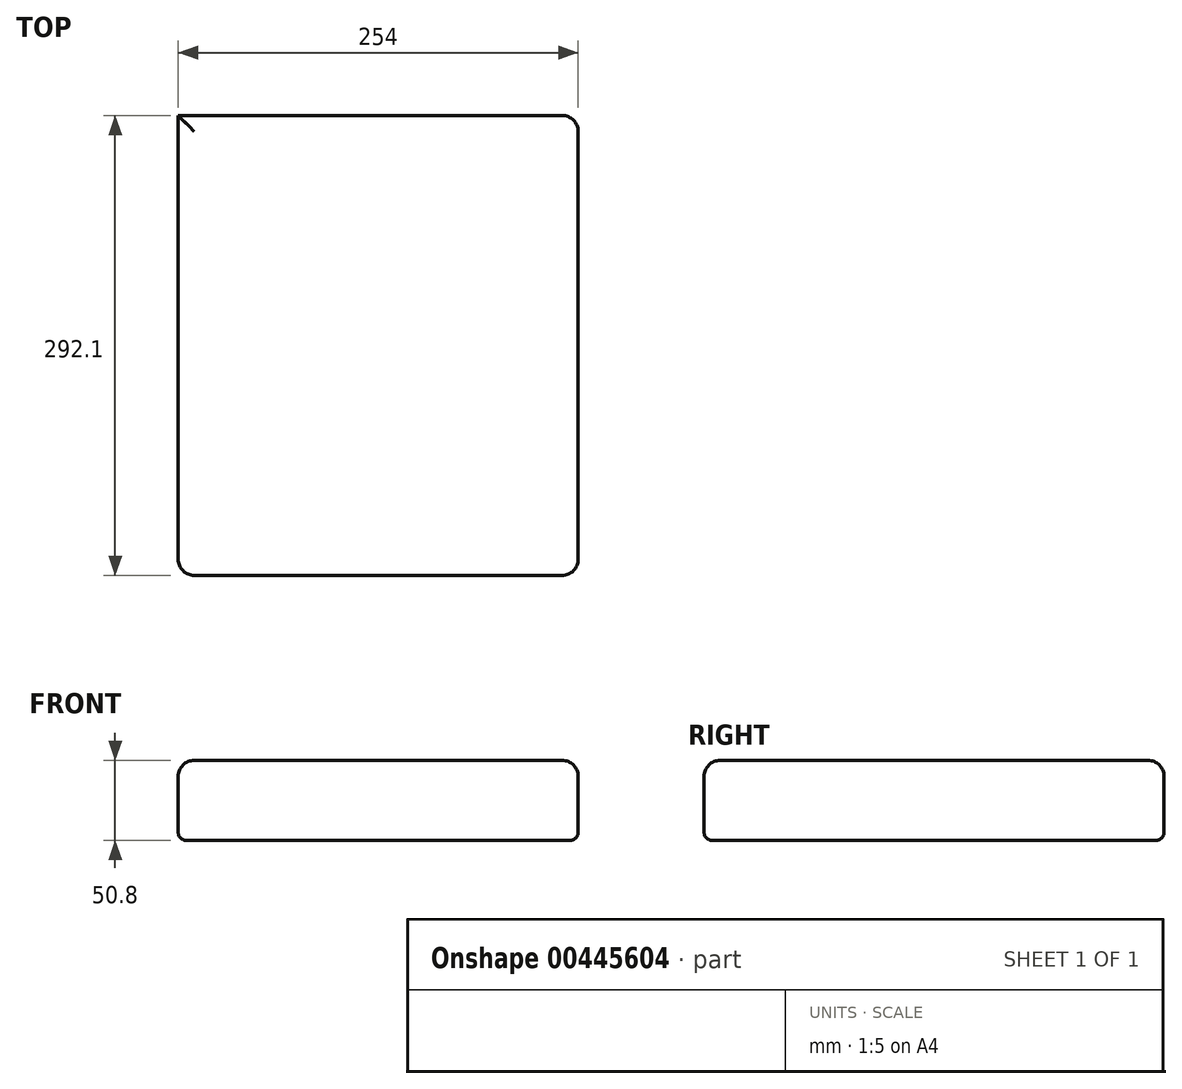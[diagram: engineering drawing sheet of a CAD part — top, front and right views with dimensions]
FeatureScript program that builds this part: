
annotation { "Feature Type Name" : "Feature", "Feature Type Description" : "" }
export const myFeature = defineFeature(function(context is Context, id is Id, definition is map)
    precondition{}
    {
        {
            var Q0;
            Q0=qCreatedBy(makeId("Top.planeOp"),FACE);
            var sketch = newSketch(context, id + "F0", { "sketchPlane" : qUnion([Q0])});
            skLineSegment(sketch, "E0.bottom", {"start": v(127, -127) * mm, "end": v(-127, -127) * mm});
            skLineSegment(sketch, "E0.top", {"start": v(127, 127) * mm, "end": v(-127, 127) * mm});
            skLineSegment(sketch, "E0.left", {"start": v(127, -127) * mm, "end": v(127, 127) * mm});
            skLineSegment(sketch, "E0.right", {"start": v(-127, -127) * mm, "end": v(-127, 127) * mm});
            skPoint(sketch, "E0.middle", {"position": v(0, 0) * mm});
            skSolve(sketch);
        }
        {
            var Q0;
            Q0 = qSketchRegion(id + "F0", true);
            extrude(context, id + "F1", {"entities" : qUnion([Q0]), "depth" : 50.8 * mm});
        }
        {
            var Q0;
            Q0=makeQuery(id+"F1.opExtrude","SWEPT_FACE",FACE,{"disambiguationData":[OSD([sQuery(id+"F0.wireOp",EDGE,"E0.bottom")])]});
            extrude(context, id + "F2", {"entities" : qUnion([Q0]), "operationType" : NewBodyOperationType.ADD, "depth" : 38.1 * mm});
        }
        {
            var Q0;
            {var subQ0=sQuery(id+"F0.wireOp",EDGE,"E0.bottom");Q0=makeQuery(id+"F2.opExtrude","CAP_EDGE",EDGE,{"disambiguationData":[OSD([subQ0]),TDD([makeQuery(id+"F1.opExtrude","CAP_EDGE",EDGE,{"disambiguationData":[OSD([subQ0])],"isStart":false})])],"isStart":false});}
            fillet(context, id + "F3", {"entities" : qUnion([Q0]), "radius" : 10.16 * mm, "tangentPropagation" : true, "allowEdgeOverflow" : false});
        }
        {
            var Q0;
            {var subQ0=sQuery(id+"F0.wireOp",EDGE,"E0.left");var subQ1=sQuery(id+"F0.wireOp",EDGE,"E0.bottom");Q0=makeQuery(id+"F2.boolean.opBoolean","MERGE",EDGE,{"derivedFrom":[makeQuery(id+"F1.opExtrude","CAP_EDGE",EDGE,{"disambiguationData":[OSD([subQ0])],"isStart":false}),makeQuery(id+"F2.opExtrude","SWEPT_EDGE",EDGE,{"disambiguationData":[OSD([subQ1,subQ0]),TDD([makeQuery(id+"F1.opExtrude","CAP_VERTEX",VERTEX,{"disambiguationData":[OSD([subQ1,subQ0])],"isStart":false})])]})]});}
            fillet(context, id + "F4", {"entities" : qUnion([Q0]), "radius" : 10.16 * mm, "tangentPropagation" : true, "allowEdgeOverflow" : false});
        }
        {
            var Q0;
            Q0=makeQuery(id+"F1.opExtrude","CAP_EDGE",EDGE,{"disambiguationData":[OSD([sQuery(id+"F0.wireOp",EDGE,"E0.top")])],"isStart":false});
            var Q1;
            {var subQ0=sQuery(id+"F0.wireOp",EDGE,"E0.right");var subQ1=sQuery(id+"F0.wireOp",EDGE,"E0.bottom");Q1=makeQuery(id+"F2.boolean.opBoolean","MERGE",EDGE,{"derivedFrom":[makeQuery(id+"F1.opExtrude","CAP_EDGE",EDGE,{"disambiguationData":[OSD([subQ0])],"isStart":false}),makeQuery(id+"F2.opExtrude","SWEPT_EDGE",EDGE,{"disambiguationData":[OSD([subQ1,subQ0]),TDD([makeQuery(id+"F1.opExtrude","CAP_VERTEX",VERTEX,{"disambiguationData":[OSD([subQ1,subQ0])],"isStart":false})])]})]});}
            fillet(context, id + "F5", {"entities" : qUnion([Q0, Q1]), "radius" : 10.16 * mm, "tangentPropagation" : true, "allowEdgeOverflow" : false});
        }
        {
            var Q0;
            {var subQ0=sQuery(id+"F0.wireOp",EDGE,"E0.right");var subQ1=sQuery(id+"F0.wireOp",EDGE,"E0.bottom");Q0=makeQuery(id+"F2.boolean.opBoolean","MERGE",EDGE,{"derivedFrom":[makeQuery(id+"F1.opExtrude","CAP_EDGE",EDGE,{"disambiguationData":[OSD([subQ0])],"isStart":true}),makeQuery(id+"F2.opExtrude","SWEPT_EDGE",EDGE,{"disambiguationData":[OSD([subQ1,subQ0]),TDD([makeQuery(id+"F1.opExtrude","CAP_VERTEX",VERTEX,{"disambiguationData":[OSD([subQ1,subQ0])],"isStart":true})])]})]});}
            var Q1;
            Q1=makeQuery(id+"F1.opExtrude","CAP_EDGE",EDGE,{"disambiguationData":[OSD([sQuery(id+"F0.wireOp",EDGE,"E0.top")])],"isStart":true});
            var Q2;
            {var subQ0=sQuery(id+"F0.wireOp",EDGE,"E0.left");var subQ1=sQuery(id+"F0.wireOp",EDGE,"E0.bottom");Q2=makeQuery(id+"F2.boolean.opBoolean","MERGE",EDGE,{"derivedFrom":[makeQuery(id+"F1.opExtrude","CAP_EDGE",EDGE,{"disambiguationData":[OSD([subQ0])],"isStart":true}),makeQuery(id+"F2.opExtrude","SWEPT_EDGE",EDGE,{"disambiguationData":[OSD([subQ1,subQ0]),TDD([makeQuery(id+"F1.opExtrude","CAP_VERTEX",VERTEX,{"disambiguationData":[OSD([subQ1,subQ0])],"isStart":true})])]})]});}
            var Q3;
            {var subQ0=sQuery(id+"F0.wireOp",EDGE,"E0.bottom");Q3=makeQuery(id+"F2.opExtrude","CAP_EDGE",EDGE,{"disambiguationData":[OSD([subQ0]),TDD([makeQuery(id+"F1.opExtrude","CAP_EDGE",EDGE,{"disambiguationData":[OSD([subQ0])],"isStart":true})])],"isStart":false});}
            fillet(context, id + "F6", {"entities" : qUnion([Q0, Q1, Q2, Q3]), "radius" : 5.08 * mm, "tangentPropagation" : true, "allowEdgeOverflow" : false});
        }
    });
